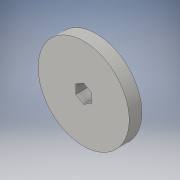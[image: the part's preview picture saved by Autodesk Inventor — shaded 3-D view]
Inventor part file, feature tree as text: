
AUTODESK INVENTOR PART (.ipt)
format: ipt  version: 2016 (Build 200138000, 138)  size: 98,304 bytes
history: native  units: in
note: dims shown in document units (in); Inventor stores cm internally (conversion verified against a paired STEP export)
features: extrude x1, sketch x1
ambient origin geometry x8: Origin, YZ Plane, XZ Plane, XY Plane, X Axis, Y Axis, Z Axis, Center Point
bodies: Solid1 (feature_tree)
feature tree (2):
  extrude  "Extrusion1"  Depth=0.5in
  sketch  "Sketch1"  dims[d0=2.875in d1=0.5in d2=0.4in d3=0.0in]
